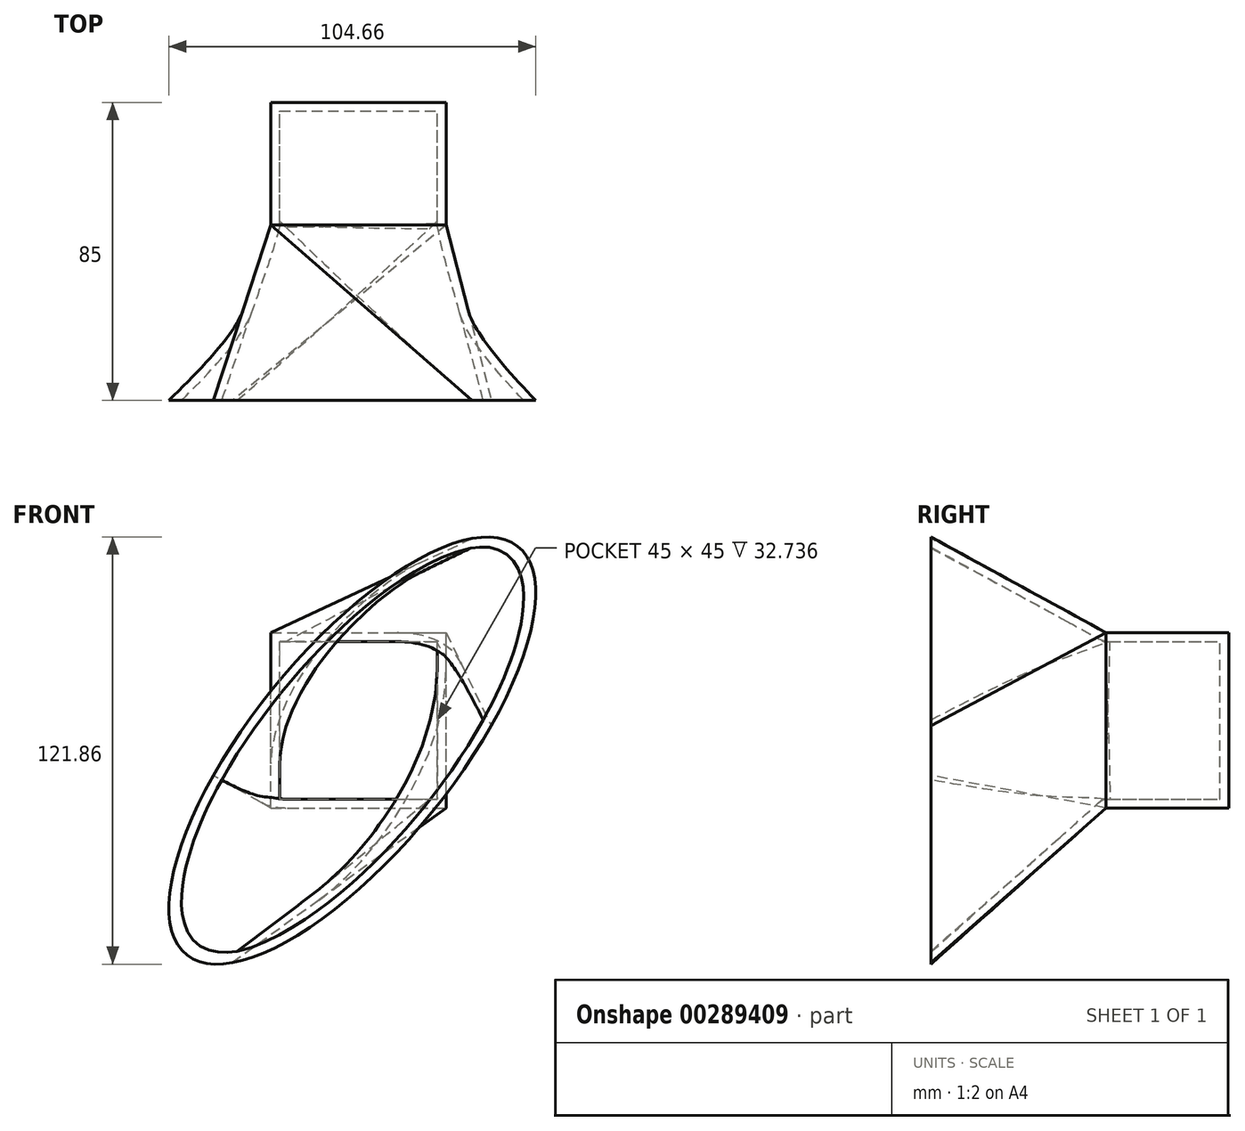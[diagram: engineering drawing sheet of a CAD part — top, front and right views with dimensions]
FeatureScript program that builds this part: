
annotation { "Feature Type Name" : "Feature", "Feature Type Description" : "" }
export const myFeature = defineFeature(function(context is Context, id is Id, definition is map)
    precondition{}
    {
        {
            var Q0;
            Q0=qCreatedBy(makeId("Front.planeOp"),FACE);
            var sketch = newSketch(context, id + "F0", { "sketchPlane" : qUnion([Q0])});
            skLineSegment(sketch, "E0.bottom", {"start": v(0, 0) * mm, "end": v(50, 0) * mm});
            skLineSegment(sketch, "E0.top", {"start": v(0, 50) * mm, "end": v(50, 50) * mm});
            skLineSegment(sketch, "E0.left", {"start": v(0, 0) * mm, "end": v(0, 50) * mm});
            skLineSegment(sketch, "E0.right", {"start": v(50, 0) * mm, "end": v(50, 50) * mm});
            skSolve(sketch);
        }
        {
            var Q0;
            Q0 = qSketchRegion(id + "F0", true);
            extrude(context, id + "F1", {"entities" : qUnion([Q0]), "depth" : 35 * mm});
        }
        {
            var Q0;
            Q0=makeQuery(id+"F1.opExtrude","CAP_FACE",FACE,{"disambiguationData":[OSD([sQuery(id+"F0.wireOp",EDGE,"E0.bottom"),sQuery(id+"F0.wireOp",EDGE,"E0.top"),sQuery(id+"F0.wireOp",EDGE,"E0.left"),sQuery(id+"F0.wireOp",EDGE,"E0.right")])],"isStart":false});
            cPlane(context, id + "F2", {"entities" : qUnion([Q0]), "cplaneType" : CPlaneType.OFFSET, "offset" : 50 * mm, "width" : 150 * mm, "height" : 150 * mm});
        }
        {
            var Q0;
            Q0=qCreatedBy(id+"F2.planeOp",FACE);
            var sketch = newSketch(context, id + "F3", { "sketchPlane" : qUnion([Q0])});
            skEllipse(sketch, "E1", {"center": v(23.21, 16.36) * mm, "majorRadius": 75 * mm, "minorRadius": 28.73 * mm, "majorAxis": v(0.63, 0.78)});
            skSolve(sketch);
        }
        {
            var Q1;
            Q1=makeQuery(id+"F1.opExtrude","CAP_FACE",FACE,{"disambiguationData":[OSD([sQuery(id+"F0.wireOp",EDGE,"E0.bottom"),sQuery(id+"F0.wireOp",EDGE,"E0.top"),sQuery(id+"F0.wireOp",EDGE,"E0.left"),sQuery(id+"F0.wireOp",EDGE,"E0.right")])],"isStart":false});
            var Q2;
            Q2=makeQuery(id+"F3.imprint","IMPRINT",FACE,{"disambiguationData":[TD([[makeQuery(id+"F3.imprint","IMPRINT",EDGE,{"derivedFrom":sQuery(id+"F3.wireOp",EDGE,"E1")}),1.0]])]});
            loft(context, id + "F4", {"operationType" : NewBodyOperationType.ADD, "sheetProfilesArray" : [{ "sheetProfileEntities" : qUnion([Q1]) }, { "sheetProfileEntities" : qUnion([Q2]) }]});
        }
        {
            var Q0;
            Q0=makeQuery(id+"F4.opLoft","CAP_FACE",FACE,{"disambiguationData":[OSD([makeQuery(id+"F3.imprint","IMPRINT",FACE,{"disambiguationData":[TD([[makeQuery(id+"F3.imprint","IMPRINT",EDGE,{"derivedFrom":sQuery(id+"F3.wireOp",EDGE,"E1")}),1.0]])]})])],"isStart":true});
            shell(context, id + "F5", {"entities" : qUnion([Q0]), "thickness" : 2.5 * mm});
        }
    });
